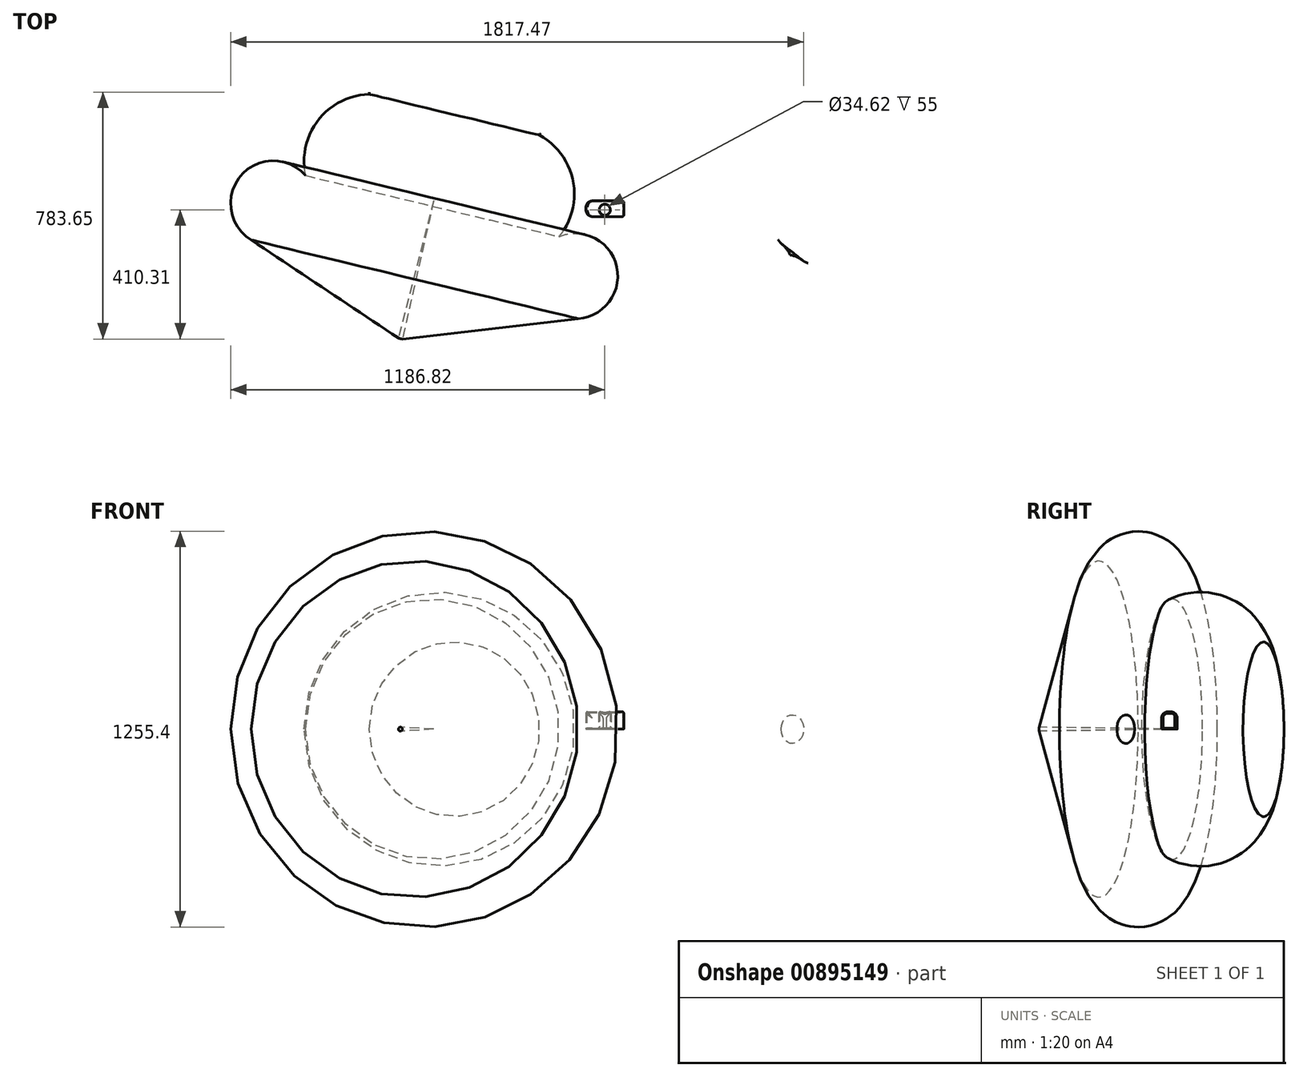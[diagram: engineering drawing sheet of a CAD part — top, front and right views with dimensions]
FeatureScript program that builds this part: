
annotation { "Feature Type Name" : "Feature", "Feature Type Description" : "" }
export const myFeature = defineFeature(function(context is Context, id is Id, definition is map)
    precondition{}
    {
        {
            var Q0;
            Q0=qCreatedBy(makeId("Top.planeOp"),FACE);
            var sketch = newSketch(context, id + "F0", { "sketchPlane" : qUnion([Q0])});
            skLineSegment(sketch, "E0.bottom", {"start": v(-98.83, 28.3) * mm, "end": v(21.17, 28.3) * mm});
            skLineSegment(sketch, "E0.top", {"start": v(-98.83, -21.7) * mm, "end": v(21.17, -21.7) * mm});
            skLineSegment(sketch, "E0.left", {"start": v(-98.83, 28.3) * mm, "end": v(-98.83, -21.7) * mm});
            skLineSegment(sketch, "E0.right", {"start": v(21.17, 28.3) * mm, "end": v(21.17, -21.7) * mm});
            skCircle(sketch, "E1", {"center": v(-39.16, 0) * mm, "radius": 17.3 * mm});
            skSolve(sketch);
        }
        {
            var Q0;
            Q0 = qSketchRegion(id + "F0", true);
            extrude(context, id + "F1", {"entities" : qUnion([Q0]), "depth" : 55 * mm, "offsetDistance" : 25 * mm});
        }
        {
            var Q0;
            Q0=makeQuery(id+"F1.opExtrude","CAP_EDGE",EDGE,{"disambiguationData":[OSD([sQuery(id+"F0.wireOp",EDGE,"E0.left")])],"isStart":false});
            fillet(context, id + "F2", {"entities" : qUnion([Q0]), "radius" : 5 * mm, "tangentPropagation" : true, "allowEdgeOverflow" : false});
        }
        {
            var Q0;
            Q0=makeQuery(id+"F1.opExtrude","CAP_EDGE",EDGE,{"disambiguationData":[OSD([sQuery(id+"F0.wireOp",EDGE,"E0.bottom")])],"isStart":false});
            fillet(context, id + "F3", {"entities" : qUnion([Q0]), "radius" : 20 * mm, "tangentPropagation" : true, "allowEdgeOverflow" : false});
        }
        {
            var Q0;
            Q0=makeQuery(id+"F1.opExtrude","CAP_EDGE",EDGE,{"disambiguationData":[OSD([sQuery(id+"F0.wireOp",EDGE,"E0.top")])],"isStart":false});
            fillet(context, id + "F4", {"entities" : qUnion([Q0]), "radius" : 20 * mm, "tangentPropagation" : true, "allowEdgeOverflow" : false});
        }
        {
            var Q0;
            Q0=makeQuery(id+"F3.opFillet","BLEND_EDGE",EDGE,{"blendedFrom":[makeQuery(id+"F1.opExtrude","CAP_EDGE",EDGE,{"disambiguationData":[OSD([sQuery(id+"F0.wireOp",EDGE,"E0.bottom")])],"isStart":false}),makeQuery(id+"F1.opExtrude","SWEPT_FACE",FACE,{"disambiguationData":[OSD([sQuery(id+"F0.wireOp",EDGE,"E0.right")])]})],"blendedInto":[makeQuery(id+"F1.opExtrude","SWEPT_FACE",FACE,{"disambiguationData":[OSD([sQuery(id+"F0.wireOp",EDGE,"E0.right")])]})]});
            var Q1;
            Q1=makeQuery(id+"F4.opFillet","BLEND_EDGE",EDGE,{"blendedFrom":[makeQuery(id+"F1.opExtrude","CAP_EDGE",EDGE,{"disambiguationData":[OSD([sQuery(id+"F0.wireOp",EDGE,"E0.top")])],"isStart":false}),makeQuery(id+"F1.opExtrude","SWEPT_FACE",FACE,{"disambiguationData":[OSD([sQuery(id+"F0.wireOp",EDGE,"E0.right")])]})],"blendedInto":[makeQuery(id+"F1.opExtrude","SWEPT_FACE",FACE,{"disambiguationData":[OSD([sQuery(id+"F0.wireOp",EDGE,"E0.right")])]})]});
            var Q2;
            Q2=makeQuery(id+"F1.opExtrude","CAP_EDGE",EDGE,{"disambiguationData":[OSD([sQuery(id+"F0.wireOp",EDGE,"E0.right")])],"isStart":false});
            fillet(context, id + "F5", {"entities" : qUnion([Q0, Q1, Q2]), "radius" : 5 * mm, "tangentPropagation" : true, "allowEdgeOverflow" : false});
        }
        {
            var Q0;
            Q0=makeQuery(id+"F1.opExtrude","SWEPT_FACE",FACE,{"disambiguationData":[OSD([sQuery(id+"F0.wireOp",EDGE,"E0.right")])]});
            shell(context, id + "F6", {"entities" : qUnion([Q0]), "thickness" : 2.5 * mm});
        }
        {
            var Q0;
            Q0=qCreatedBy(makeId("Top.planeOp"),FACE);
            var sketch = newSketch(context, id + "F7", { "sketchPlane" : qUnion([Q0])});
            skArc(sketch, "E2", {"start": v(591.5, -163.23) * mm, "mid": v(716.11, -120.38) * mm, "end": v(662.5, 0) * mm});
            skArc(sketch, "E3", {"start": v(450.34, -268.11) * mm, "mid": v(587.12, -304.77) * mm, "end": v(591.5, -163.23) * mm});
            skLineSegment(sketch, "E4", {"start": v(662.5, 0) * mm, "end": v(450.34, -268.11) * mm});
            skSolve(sketch);
        }
        {
            var Q0;
            Q0=makeQuery(id+"F7.imprint","IMPRINT",FACE,{"disambiguationData":[TD([[makeQuery(id+"F7.imprint","IMPRINT",EDGE,{"derivedFrom":sQuery(id+"F7.wireOp",EDGE,"E2")}),1.0]])]});
            var Q1;
            Q1=sQuery(id+"F7.wireOp",EDGE,"E4");
            revolve(context, id + "F8", {"surfaceOperationType" : NewSurfaceOperationType.NEW, "entities" : qUnion([Q0]), "axis" : qUnion([Q1]), "revolveType" : RevolveType.FULL});
        }
        {
            var Q0;
            Q0=qCreatedBy(makeId("Top.planeOp"),FACE);
            var sketch = newSketch(context, id + "F9", { "sketchPlane" : qUnion([Q0])});
            skArc(sketch, "E5", {"start": v(-246.77, 236.84) * mm, "mid": v(-300.2, 435.96) * mm, "end": v(-498.03, 377.97) * mm});
            skLineSegment(sketch, "E6", {"start": v(-498.03, 377.97) * mm, "end": v(-581.99, 29.35) * mm});
            skLineSegment(sketch, "E7", {"start": v(-581.99, 29.35) * mm, "end": v(-681.3, -410.31) * mm});
            skArc(sketch, "E8", {"start": v(-184.52, -85.05) * mm, "mid": v(-139.72, 90.58) * mm, "end": v(-246.77, 236.84) * mm});
            skArc(sketch, "E9", {"start": v(-123.5, -345.43) * mm, "mid": v(-1.53, -179.5) * mm, "end": v(-184.52, -85.05) * mm});
            skLineSegment(sketch, "E10", {"start": v(-123.5, -345.43) * mm, "end": v(-681.3, -410.31) * mm});
            skSolve(sketch);
        }
        {
            var Q0;
            Q0=makeQuery(id+"F9.imprint","IMPRINT",FACE,{"disambiguationData":[TD([[makeQuery(id+"F9.imprint","IMPRINT",EDGE,{"derivedFrom":sQuery(id+"F9.wireOp",EDGE,"E5")}),1.0]])]});
            var Q1;
            Q1=sQuery(id+"F9.wireOp",EDGE,"E6");
            revolve(context, id + "F10", {"surfaceOperationType" : NewSurfaceOperationType.NEW, "entities" : qUnion([Q0]), "axis" : qUnion([Q1]), "revolveType" : RevolveType.FULL});
        }
    });
